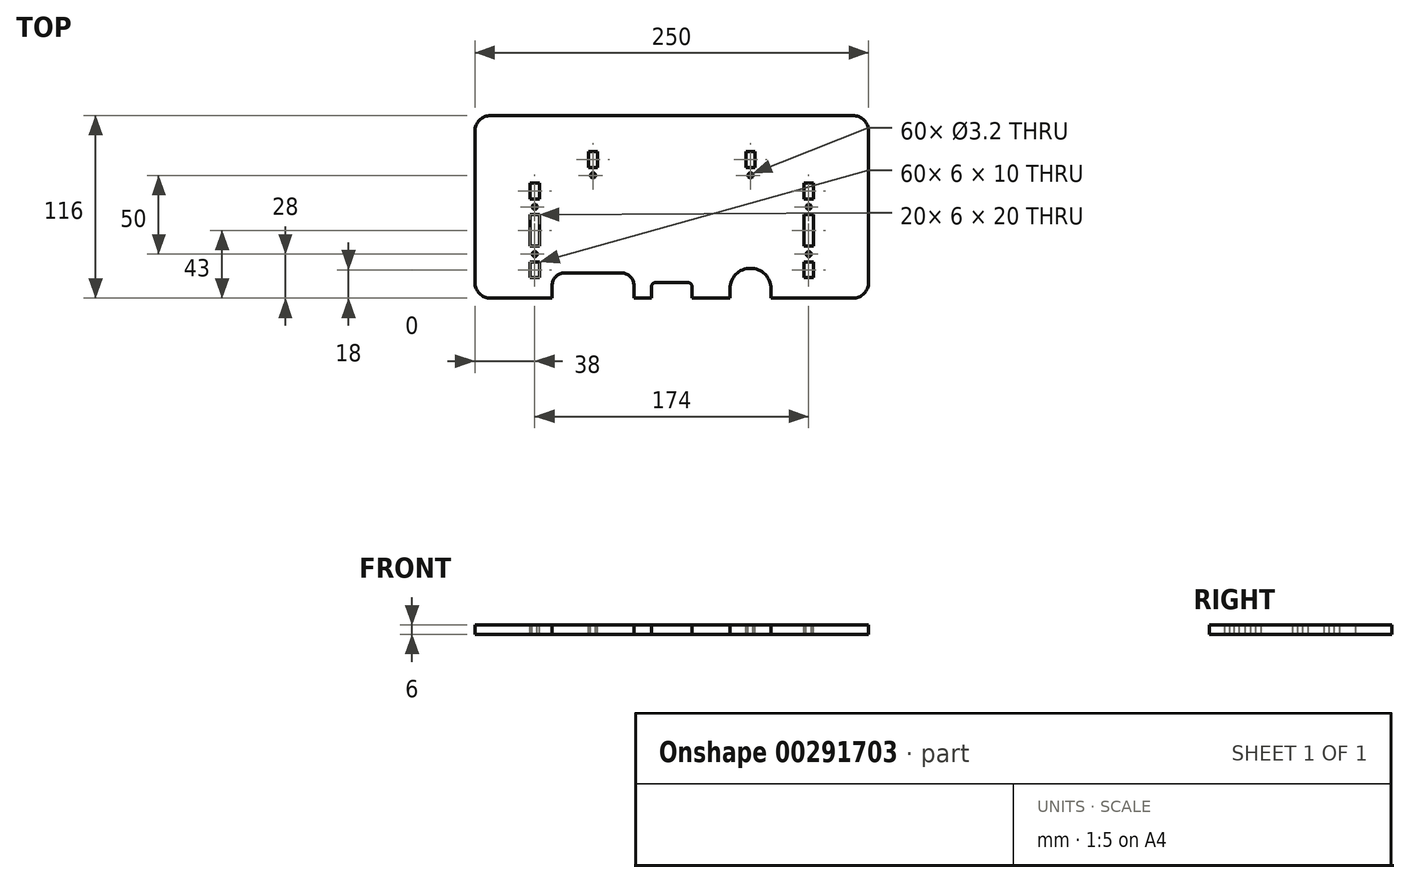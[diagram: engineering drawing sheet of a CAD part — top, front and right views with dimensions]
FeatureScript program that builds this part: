
annotation { "Feature Type Name" : "Feature", "Feature Type Description" : "" }
export const myFeature = defineFeature(function(context is Context, id is Id, definition is map)
    precondition{}
    {
        {
            var Q0;
            Q0=qCreatedBy(makeId("Top.planeOp"),FACE);
            var sketch = newSketch(context, id + "F0", { "sketchPlane" : qUnion([Q0])});
            skLineSegment(sketch, "E0.bottom", {"start": v(125, -58) * mm, "end": v(-125, -58) * mm});
            skLineSegment(sketch, "E0.top", {"start": v(125, 58) * mm, "end": v(-125, 58) * mm});
            skLineSegment(sketch, "E0.left", {"start": v(125, -58) * mm, "end": v(125, 58) * mm});
            skLineSegment(sketch, "E0.right", {"start": v(-125, -58) * mm, "end": v(-125, 58) * mm});
            skPoint(sketch, "E0.middle", {"position": v(0, 0) * mm});
            skSolve(sketch);
        }
        {
            var Q0;
            Q0=qSketchRegion(id+"F0",true);
            extrude(context, id + "F1", {"entities" : qUnion([Q0]), "depth" : 6 * mm});
        }
        {
            var Q0;
            Q0=makeQuery(id+"F1.opExtrude","CAP_FACE",FACE,{"disambiguationData":[OSD([sQuery(id+"F0.wireOp",EDGE,"E0.bottom"),sQuery(id+"F0.wireOp",EDGE,"E0.top"),sQuery(id+"F0.wireOp",EDGE,"E0.left"),sQuery(id+"F0.wireOp",EDGE,"E0.right")])],"isStart":false});
            var sketch = newSketch(context, id + "F2", { "sketchPlane" : qUnion([Q0])});
            skLineSegment(sketch, "E1", {"start": v(0, 58) * mm, "end": v(0, -58) * mm, "construction": true});
            skLineSegment(sketch, "E2", {"start": v(-125, -15) * mm, "end": v(125, -15) * mm, "construction": true});
            skLineSegment(sketch, "E3", {"start": v(-90, 58) * mm, "end": v(-90, -58) * mm, "construction": true});
            skLineSegment(sketch, "E4.bottom", {"start": v(-90, -35) * mm, "end": v(-84, -35) * mm});
            skLineSegment(sketch, "E4.top", {"start": v(-90, -45) * mm, "end": v(-84, -45) * mm});
            skLineSegment(sketch, "E4.left", {"start": v(-90, -35) * mm, "end": v(-90, -45) * mm});
            skLineSegment(sketch, "E4.right", {"start": v(-84, -35) * mm, "end": v(-84, -45) * mm});
            skLineSegment(sketch, "E5.MirrorCS", {"start": v(-90, 5) * mm, "end": v(-84, 5) * mm});
            skLineSegment(sketch, "E6.MirrorCS", {"start": v(-90, 15) * mm, "end": v(-84, 15) * mm});
            skLineSegment(sketch, "E7.MirrorCS", {"start": v(-84, 5) * mm, "end": v(-84, 15) * mm});
            skLineSegment(sketch, "E8.MirrorCS", {"start": v(-90, 5) * mm, "end": v(-90, 15) * mm});
            skLineSegment(sketch, "E9.MirrorCS", {"start": v(90, -45) * mm, "end": v(84, -45) * mm});
            skLineSegment(sketch, "E10.MirrorCS", {"start": v(90, -35) * mm, "end": v(84, -35) * mm});
            skLineSegment(sketch, "E11.MirrorCS", {"start": v(90, -35) * mm, "end": v(90, -45) * mm});
            skLineSegment(sketch, "E12.MirrorCS", {"start": v(84, 5) * mm, "end": v(84, 15) * mm});
            skLineSegment(sketch, "E13.MirrorCS", {"start": v(84, -35) * mm, "end": v(84, -45) * mm});
            skLineSegment(sketch, "E14.MirrorCS", {"start": v(90, 5) * mm, "end": v(90, 15) * mm});
            skLineSegment(sketch, "E15.MirrorCS", {"start": v(90, 5) * mm, "end": v(84, 5) * mm});
            skLineSegment(sketch, "E16.MirrorCS", {"start": v(90, 15) * mm, "end": v(84, 15) * mm});
            skLineSegment(sketch, "E17", {"start": v(-90, -5) * mm, "end": v(-90, -25) * mm});
            skLineSegment(sketch, "E18", {"start": v(-90, -25) * mm, "end": v(-84, -25) * mm});
            skLineSegment(sketch, "E19", {"start": v(-84, -25) * mm, "end": v(-84, -5) * mm});
            skLineSegment(sketch, "E20", {"start": v(-84, -5) * mm, "end": v(-90, -5) * mm});
            skPoint(sketch, "E21", {"position": v(-90, -15) * mm});
            skLineSegment(sketch, "E22.MirrorCS", {"start": v(90, -5) * mm, "end": v(90, -25) * mm});
            skPoint(sketch, "E23.MirrorP", {"position": v(90, -15) * mm});
            skLineSegment(sketch, "E24.MirrorCS", {"start": v(84, -25) * mm, "end": v(84, -5) * mm});
            skLineSegment(sketch, "E25.MirrorCS", {"start": v(84, -5) * mm, "end": v(90, -5) * mm});
            skLineSegment(sketch, "E26.MirrorCS", {"start": v(90, -25) * mm, "end": v(84, -25) * mm});
            skLineSegment(sketch, "E27", {"start": v(13, -58) * mm, "end": v(-13, -58) * mm});
            skLineSegment(sketch, "E28", {"start": v(-13, -58) * mm, "end": v(-13, -48) * mm});
            skLineSegment(sketch, "E29", {"start": v(-13, -48) * mm, "end": v(13, -48) * mm});
            skLineSegment(sketch, "E30", {"start": v(13, -48) * mm, "end": v(13, -58) * mm});
            skLineSegment(sketch, "E31", {"start": v(-87, -25) * mm, "end": v(-87, -35) * mm, "construction": true});
            skCircle(sketch, "E32", {"center": v(-87, -30) * mm, "radius": 1.6 * mm});
            skCircle(sketch, "E33.MirrorC", {"center": v(-87, 0) * mm, "radius": 1.6 * mm});
            skCircle(sketch, "E34.MirrorC", {"center": v(87, -30) * mm, "radius": 1.6 * mm});
            skCircle(sketch, "E35.MirrorC", {"center": v(87, 0) * mm, "radius": 1.6 * mm});
            skLineSegment(sketch, "E36", {"start": v(50, -15) * mm, "end": v(50, -58) * mm, "construction": true});
            skLineSegment(sketch, "E37", {"start": v(-50, -15) * mm, "end": v(-50, -58) * mm, "construction": true});
            skLineSegment(sketch, "E38", {"start": v(63, -58) * mm, "end": v(63, -52) * mm});
            skArc(sketch, "E39", {"start": v(63, -52) * mm, "mid": v(50, -39) * mm, "end": v(37, -52) * mm});
            skLineSegment(sketch, "E40", {"start": v(37, -52) * mm, "end": v(37, -58) * mm});
            skLineSegment(sketch, "E41", {"start": v(37, -58) * mm, "end": v(63, -58) * mm});
            skLineSegment(sketch, "E42", {"start": v(-24, -58) * mm, "end": v(-24, -42) * mm});
            skLineSegment(sketch, "E43", {"start": v(-24, -42) * mm, "end": v(-76, -42) * mm});
            skLineSegment(sketch, "E44", {"start": v(-76, -42) * mm, "end": v(-76, -58) * mm});
            skLineSegment(sketch, "E45", {"start": v(-76, -58) * mm, "end": v(-24, -58) * mm});
            skSolve(sketch);
        }
        {
            var Q0;
            Q0=qSketchRegion(id+"F2",true);
            extrude(context, id + "F3", {"entities" : qUnion([Q0]), "operationType" : NewBodyOperationType.REMOVE, "endBound" : BoundingType.THROUGH_ALL, "oppositeDirection" : true, "depth" : 25 * mm});
        }
        {
            var Q0;
            Q0=makeQuery(id+"F3.boolean.opBoolean","COPY",EDGE,{"derivedFrom":makeQuery(id+"F3.opExtrude","SWEPT_EDGE",EDGE,{"disambiguationData":[OSD([sQuery(id+"F2.wireOp",EDGE,"E28"),sQuery(id+"F2.wireOp",EDGE,"E29")])]})});
            var Q1;
            Q1=makeQuery(id+"F3.boolean.opBoolean","COPY",EDGE,{"derivedFrom":makeQuery(id+"F3.opExtrude","SWEPT_EDGE",EDGE,{"disambiguationData":[OSD([sQuery(id+"F2.wireOp",EDGE,"E29"),sQuery(id+"F2.wireOp",EDGE,"E30")])]})});
            var Q2;
            Q2=makeQuery(id+"F3.boolean.opBoolean","COPY",EDGE,{"derivedFrom":makeQuery(id+"F3.opExtrude","SWEPT_EDGE",EDGE,{"disambiguationData":[OSD([sQuery(id+"F0.wireOp",EDGE,"E0.bottom"),sQuery(id+"F2.wireOp",EDGE,"E27"),sQuery(id+"F2.wireOp",EDGE,"E28")])]})});
            var Q3;
            Q3=makeQuery(id+"F3.boolean.opBoolean","COPY",EDGE,{"derivedFrom":makeQuery(id+"F3.opExtrude","SWEPT_EDGE",EDGE,{"disambiguationData":[OSD([sQuery(id+"F0.wireOp",EDGE,"E0.bottom"),sQuery(id+"F2.wireOp",EDGE,"E27"),sQuery(id+"F2.wireOp",EDGE,"E30")])]})});
            fillet(context, id + "F4", {"entities" : qUnion([Q0, Q1, Q2, Q3]), "radius" : 3 * mm, "tangentPropagation" : true, "allowEdgeOverflow" : false});
        }
        {
            var Q0;
            Q0=makeQuery(id+"F1.opExtrude","SWEPT_EDGE",EDGE,{"disambiguationData":[OSD([sQuery(id+"F0.wireOp",EDGE,"E0.bottom"),sQuery(id+"F0.wireOp",EDGE,"E0.right")])]});
            var Q1;
            Q1=makeQuery(id+"F1.opExtrude","SWEPT_EDGE",EDGE,{"disambiguationData":[OSD([sQuery(id+"F0.wireOp",EDGE,"E0.bottom"),sQuery(id+"F0.wireOp",EDGE,"E0.left")])]});
            var Q2;
            Q2=makeQuery(id+"F1.opExtrude","SWEPT_EDGE",EDGE,{"disambiguationData":[OSD([sQuery(id+"F0.wireOp",EDGE,"E0.top"),sQuery(id+"F0.wireOp",EDGE,"E0.left")])]});
            var Q3;
            Q3=makeQuery(id+"F1.opExtrude","SWEPT_EDGE",EDGE,{"disambiguationData":[OSD([sQuery(id+"F0.wireOp",EDGE,"E0.top"),sQuery(id+"F0.wireOp",EDGE,"E0.right")])]});
            fillet(context, id + "F5", {"entities" : qUnion([Q0, Q1, Q2, Q3]), "radius" : 10 * mm, "tangentPropagation" : true, "allowEdgeOverflow" : false});
        }
        {
            var Q0;
            Q0=makeQuery(id+"F3.boolean.opBoolean","COPY",EDGE,{"derivedFrom":makeQuery(id+"F3.opExtrude","SWEPT_EDGE",EDGE,{"disambiguationData":[OSD([sQuery(id+"F0.wireOp",EDGE,"E0.bottom"),sQuery(id+"F2.wireOp",EDGE,"E40"),sQuery(id+"F2.wireOp",EDGE,"E41")])]})});
            var Q1;
            Q1=makeQuery(id+"F3.boolean.opBoolean","COPY",EDGE,{"derivedFrom":makeQuery(id+"F3.opExtrude","SWEPT_EDGE",EDGE,{"disambiguationData":[OSD([sQuery(id+"F0.wireOp",EDGE,"E0.bottom"),sQuery(id+"F2.wireOp",EDGE,"E38"),sQuery(id+"F2.wireOp",EDGE,"E41")])]})});
            var Q2;
            Q2=makeQuery(id+"F3.boolean.opBoolean","COPY",EDGE,{"derivedFrom":makeQuery(id+"F3.opExtrude","SWEPT_EDGE",EDGE,{"disambiguationData":[OSD([sQuery(id+"F0.wireOp",EDGE,"E0.bottom"),sQuery(id+"F2.wireOp",EDGE,"E42"),sQuery(id+"F2.wireOp",EDGE,"E45")])]})});
            var Q3;
            Q3=makeQuery(id+"F3.boolean.opBoolean","COPY",EDGE,{"derivedFrom":makeQuery(id+"F3.opExtrude","SWEPT_EDGE",EDGE,{"disambiguationData":[OSD([sQuery(id+"F2.wireOp",EDGE,"E42"),sQuery(id+"F2.wireOp",EDGE,"E43")])]})});
            var Q4;
            Q4=makeQuery(id+"F3.boolean.opBoolean","COPY",EDGE,{"derivedFrom":makeQuery(id+"F3.opExtrude","SWEPT_EDGE",EDGE,{"disambiguationData":[OSD([sQuery(id+"F2.wireOp",EDGE,"E43"),sQuery(id+"F2.wireOp",EDGE,"E44")])]})});
            var Q5;
            Q5=makeQuery(id+"F3.boolean.opBoolean","COPY",EDGE,{"derivedFrom":makeQuery(id+"F3.opExtrude","SWEPT_EDGE",EDGE,{"disambiguationData":[OSD([sQuery(id+"F0.wireOp",EDGE,"E0.bottom"),sQuery(id+"F2.wireOp",EDGE,"E44"),sQuery(id+"F2.wireOp",EDGE,"E45")])]})});
            fillet(context, id + "F6", {"entities" : qUnion([Q0, Q1, Q2, Q3, Q4, Q5]), "radius" : 8 * mm, "tangentPropagation" : true, "allowEdgeOverflow" : false});
        }
        {
            var Q0;
            Q0=makeQuery(id+"F1.opExtrude","CAP_FACE",FACE,{"disambiguationData":[OSD([sQuery(id+"F0.wireOp",EDGE,"E0.bottom"),sQuery(id+"F0.wireOp",EDGE,"E0.top"),sQuery(id+"F0.wireOp",EDGE,"E0.left"),sQuery(id+"F0.wireOp",EDGE,"E0.right")])],"isStart":false});
            var sketch = newSketch(context, id + "F7", { "sketchPlane" : qUnion([Q0])});
            skLineSegment(sketch, "E46", {"start": v(-84, -15) * mm, "end": v(84, -15) * mm, "construction": true});
            skLineSegment(sketch, "E47", {"start": v(-50, 20) * mm, "end": v(50, 20) * mm, "construction": true});
            skLineSegment(sketch, "E48", {"start": v(0, -15) * mm, "end": v(0, 58) * mm, "construction": true});
            skPoint(sketch, "E49", {"position": v(0, 20) * mm});
            skCircle(sketch, "E50", {"center": v(-50, 20) * mm, "radius": 1.6 * mm});
            skLineSegment(sketch, "E51", {"start": v(-50, 20) * mm, "end": v(-50, 35) * mm, "construction": true});
            skLineSegment(sketch, "E52.bottom", {"start": v(-53, 35) * mm, "end": v(-47, 35) * mm});
            skLineSegment(sketch, "E52.top", {"start": v(-53, 25) * mm, "end": v(-47, 25) * mm});
            skLineSegment(sketch, "E52.left", {"start": v(-53, 35) * mm, "end": v(-53, 25) * mm});
            skLineSegment(sketch, "E52.right", {"start": v(-47, 35) * mm, "end": v(-47, 25) * mm});
            skLineSegment(sketch, "E53.MirrorCS", {"start": v(47, 35) * mm, "end": v(47, 25) * mm});
            skLineSegment(sketch, "E54.MirrorCS", {"start": v(53, 35) * mm, "end": v(53, 25) * mm});
            skLineSegment(sketch, "E55.MirrorCS", {"start": v(53, 25) * mm, "end": v(47, 25) * mm});
            skLineSegment(sketch, "E56.MirrorCS", {"start": v(53, 35) * mm, "end": v(47, 35) * mm});
            skCircle(sketch, "E57.MirrorC", {"center": v(50, 20) * mm, "radius": 1.6 * mm});
            skSolve(sketch);
        }
        {
            var Q0;
            Q0=qSketchRegion(id+"F7",true);
            extrude(context, id + "F8", {"entities" : qUnion([Q0]), "operationType" : NewBodyOperationType.REMOVE, "endBound" : BoundingType.THROUGH_ALL, "oppositeDirection" : true, "depth" : 25 * mm});
        }
    });
